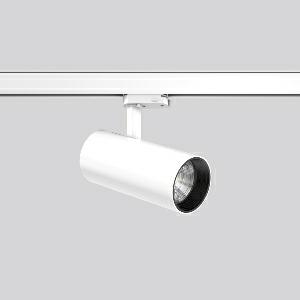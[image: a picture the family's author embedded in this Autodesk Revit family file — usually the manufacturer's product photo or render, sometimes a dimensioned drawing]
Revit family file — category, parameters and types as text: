
# Revit family: deecos_s_mini_742199_002_3_5d02
name_source: partatom
category: Lighting Fixtures
units: mm (PartAtom-declared; Revit-internal decimal feet)

## family parameters
Cut with Voids When Loaded = No
Host = Face
Light Source = No
Part Type = Normal
Room Calculation Point = No
Round Connector Dimension = Use Diameter
Shared = No

## types (1)
- DEECOS S mini (1 x LED Modul 935, 2150 lm, 3500)
    Apparent Load = 20 VA
    Approval mark = CE
    CIE Flux Codes = 96 100 100 100 100
    Color Rendering = 92
    Color Temperature = 3500
    Default Elevation = 1800 mm
    Description = Series: DEECOS S mini
LED surface-mounted projector in modern design with no visible cooling ribs. Housing: die-cast aluminium, powder-coated. Rotation range: 356°. Swivel range: 90°. Black plastic ring and recessed LED to prevent glare from the side. Optical assembly with lens made of plastic (polycarbonate) for the best homogeneous light distribution - can be changed without tools. Best colour rendering index Ra>90. With multi adaptor for 3-circuit tracks 230 V. Suitable for Track on ceiling, Wall track. High quality converter without flickering and stroboscopic effect. The following accessories can be mounted without use of tools: interchangeable lenses, decorative glasses, honeycomb louvre, clear and frosted diffusers, white interchangeable plastic ring. 
Colour: traffic white, matt (RAL 9016)
Diameter: 87 mm
Height: 214 mm
Lamp: LED
Socket: without socket
Colour temperature: 3500K
Colour rendering index (CRI): 92
System power: 20 W
Rated luminous flux: 2150 lm
Luminous efficiency: 108 lm/W
Control gear: Regulated power supply
Protection class: I
Type of protection: IP 20
    Height = 214 mm
    Lamp = 1 x LED Modul 935
    Lamp Light Flux = 2150 lm
    Lamp count = 1
    Length = 87 mm
    Lifetime = 50000 h
    Luminous efficacy = 108 lm/W
    Manufacturer = RZB
    ModVariant = No
    Model = 742199.002.3
    Mounting Place = Ceiling
    Mounting Type = Rail mounted
    Number of Poles = 1
    OnlyDefault = Yes
    Power Factor = 1
    Product Name = DEECOS S mini
    Product group = Track mounted projectors
    ProductGroupID = 301
    Protection Class = Protection class I
    Protection Degree = IP 20
    RLX_Detail_Level = 1
    RLX_Emergency_Light_Flux = 0 lm
    RLX_Emergency_Type = 0
    RLX_Emergency_Type_DB = No
    RlxData = <blob elided: 35357 chars, md5=c7912a5a>
    Socket = socket
    Standby Power = 0 W
    System Light Flux = 2150 lm
    System Power = 20 W
    Type Comments = Product without accessories
    Type Image = 741930.002.jpg
    URL = http://relux.com
    VarID = ---
    Voltage = 230 V
    Voltage Range = 220-240 V
    Weight = 0.00 kg
    Width = 0 mm  [stored 0 ft]

note: [stored X ft] marks values corroborated as IEEE doubles in the binary element streams (Revit-internal decimal feet)

## geometry (parser evidence)
native form markers: Blend x4, Sweep x13
no freeform markers — native parametric forms only
